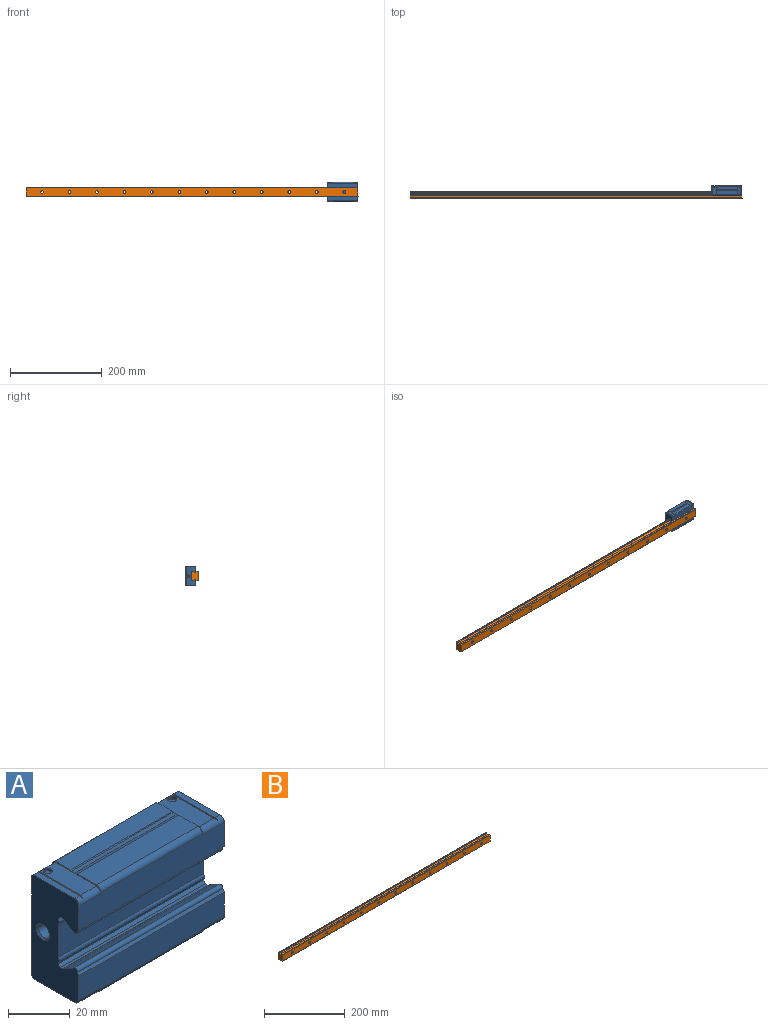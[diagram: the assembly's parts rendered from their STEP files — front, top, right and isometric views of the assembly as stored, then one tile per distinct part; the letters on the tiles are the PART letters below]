
ASSEMBLY  parts=2 mates=1
PART A: 104 faces, bbox 66.5x22x42 mm
  f0: plane 18.8x2.25mm, normal (0,0,1), area 42.3mm2, adj f1,f31,f77,f103
  f1: cylinder r=2mm len=9.95mm, axis (-1,0,0), area 30.8mm2, adj f0,f2,f29,f31,f41,f77,f100
  f2: plane 18.8x7.2mm, normal (0,0,1), area 128.3mm2, adj f1,f41,f86,f100,f102
  f3: plane 7.6x0.8mm, normal (0,0.71,-0.71), area 8.4mm2, adj f5,f8,f24,f41,f101
  f4: plane 2.25x0.8mm, normal (0,0.71,-0.71), area 2.5mm2, adj f7,f25,f31,f77
  f5: plane 18.8x7.2mm, normal (0,0,-1), area 128.3mm2, adj f3,f6,f41,f90,f101
  f6: cylinder r=2mm len=9.95mm, axis (-1,0,0), area 30.8mm2, adj f5,f7,f28,f31,f41,f77,f101
  f7: plane 18.8x2.25mm, normal (0,0,-1), area 42.3mm2, adj f4,f6,f31,f77
  f8: plane 40.4x0.5mm, normal (0.71,0.71,0), area 28.3mm2, adj f3,f24,f77,f100,f101,f102
  f9: plane 2.25x0.8mm, normal (0,0.71,-0.71), area 2.5mm2, adj f17,f26,f30,f76
  f10: plane 7.6x0.8mm, normal (0,0.71,-0.71), area 8.4mm2, adj f18,f19,f27,f42,f98
  f11: plane 7.6x0.8mm, normal (0,0.71,0.71), area 8.4mm2, adj f13,f19,f27,f42,f99
  f12: plane 2.25x0.8mm, normal (0,0.71,0.71), area 2.5mm2, adj f14,f26,f30,f76
  f13: plane 18.8x7.2mm, normal (0,0,1), area 128.3mm2, adj f11,f15,f42,f84,f99
  f14: plane 18.8x2.25mm, normal (0,0,1), area 42.3mm2, adj f12,f15,f30,f76
  f15: cylinder r=2mm len=9.95mm, axis (1,0,0), area 30.8mm2, adj f13,f14,f29,f30,f42,f76,f99
  f16: cylinder r=2mm len=9.95mm, axis (1,0,0), area 30.8mm2, adj f17,f18,f28,f30,f42,f76,f98
  f17: plane 18.8x2.25mm, normal (0,0,-1), area 42.3mm2, adj f9,f16,f30,f76
  f18: plane 18.8x7.2mm, normal (0,0,-1), area 128.3mm2, adj f10,f16,f42,f88,f98
  f19: plane 40.4x0.5mm, normal (-0.71,0.71,0), area 28.3mm2, adj f10,f11,f27,f76,f98,f99
  f20: plane 46.6x8.82mm, normal (0,0,1), area 411mm2, adj f33,f41,f42,f95
  f21: plane 46.6x7.1mm, normal (0,0,1), area 330.9mm2, adj f32,f41,f42,f97
  f22: plane 46.6x8.82mm, normal (0,0,-1), area 411mm2, adj f34,f41,f42,f93
  f23: plane 46.6x7.1mm, normal (0,0,-1), area 330.9mm2, adj f35,f41,f42,f94
  f24: plane 39.6x7.2mm, normal (0,1,0), area 285.1mm2, adj f3,f8,f41,f102
  f25: plane 39.6x2.25mm, normal (0,1,0), area 89.1mm2, adj f4,f31,f77,f103
  f26: plane 39.6x2.25mm, normal (0,1,0), area 89.1mm2, adj f9,f12,f30,f76
  f27: plane 39.6x7.2mm, normal (0,1,0), area 285.1mm2, adj f10,f11,f19,f42
  f28: plane 66.5x9.96mm, normal (0,-1,0), area 654.6mm2, adj f6,f16,f30,f31,f34,f41,f42,f55
  f29: plane 66.5x9.96mm, normal (0,-1,0), area 654.6mm2, adj f1,f15,f30,f31,f33,f41,f42,f56
  f30: plane 41.2x21.6mm, normal (-1,0,0), area 698.5mm2, adj f9,f12,f14,f15,f16,f17,f26,f28
  f31: plane 41.2x21.6mm, normal (1,0,0), area 698.5mm2, adj f0,f1,f4,f6,f7,f25,f28,f29
  f32: plane 46.6x1.1mm, normal (0,0.71,0.71), area 72.5mm2, adj f21,f40,f41,f42
  f33: cylinder r=2mm len=46.6mm, axis (1,0,0), area 146.4mm2, adj f20,f29,f41,f42
  f34: cylinder r=2mm len=46.6mm, axis (1,0,0), area 146.4mm2, adj f22,f28,f41,f42
  f35: plane 46.6x1.1mm, normal (0,0.71,-0.71), area 72.5mm2, adj f23,f36,f41,f42
  f36: plane 46.6x14.35mm, normal (0,1,0), area 629.4mm2, adj f35,f37,f41,f42,f49,f52
  f37: plane 46.6x0.3mm, normal (0,0.71,0.71), area 19.8mm2, adj f36,f38,f41,f42
  f38: plane 46.6x10.5mm, normal (0,1,0), area 489.3mm2, adj f37,f39,f41,f42
  f39: plane 46.6x0.3mm, normal (0,0.71,-0.71), area 19.8mm2, adj f38,f40,f41,f42
  f40: plane 46.6x14.35mm, normal (0,1,0), area 629.4mm2, adj f32,f39,f41,f42,f43,f46
  f41: plane 42x22mm, normal (1,0,0), area 28.8mm2, adj f1,f2,f3,f5,f6,f20,f21,f22
  f42: plane 42x22mm, normal (-1,0,0), area 28.8mm2, adj f10,f11,f13,f15,f16,f18,f20,f21
  f43: cone r=2.5mm half-angle=45deg, axis (0,1,0), area 8.8mm2, adj f40,f44
  f44: cylinder r=2.07mm len=9.17mm, axis (0,1,0), area 119.1mm2, adj f43,f45
  f45: cone r=2.07mm half-angle=60deg, axis (0,1,0), area 15.5mm2, adj f44
  f46: cone r=2.5mm half-angle=45deg, axis (0,1,0), area 8.8mm2, adj f40,f47
  f47: cylinder r=2.07mm len=9.17mm, axis (0,1,0), area 119.1mm2, adj f46,f48
  f48: cone r=2.07mm half-angle=60deg, axis (0,1,0), area 15.5mm2, adj f47
  f49: cone r=2.5mm half-angle=45deg, axis (0,1,0), area 8.8mm2, adj f36,f50
  f50: cylinder r=2.07mm len=9.17mm, axis (0,1,0), area 119.1mm2, adj f49,f51
  f51: cone r=2.07mm half-angle=60deg, axis (0,1,0), area 15.5mm2, adj f50
  f52: cone r=2.5mm half-angle=45deg, axis (0,1,0), area 8.8mm2, adj f36,f53
  f53: cylinder r=2.07mm len=9.17mm, axis (0,1,0), area 119.1mm2, adj f52,f54
  f54: cone r=2.07mm half-angle=60deg, axis (0,1,0), area 15.5mm2, adj f53
  f55: plane 66.5x0.92mm, normal (0,-0.8,0.6), area 76.7mm2, adj f28,f30,f31,f57
  f56: plane 66.5x0.92mm, normal (0,-0.8,-0.6), area 76.7mm2, adj f29,f30,f31,f75
  f57: cylinder r=1mm len=66.5mm, axis (1,0,0), area 165mm2, adj f30,f31,f55,f58
  f58: cylinder r=0.7mm len=66.5mm, axis (1,0,0), area 5.3mm2, adj f30,f31,f57,f59
  f59: plane 66.5x3.35mm, normal (0,0.5,0.87), area 257.1mm2, adj f30,f31,f58,f60
  f60: cylinder r=1.65mm len=66.5mm, axis (1,0,0), area 87.9mm2, adj f30,f31,f59,f61
  f61: plane 66.5x0.59mm, normal (0,0.5,0.87), area 45.2mm2, adj f30,f31,f60,f62
  f62: plane 66.5x1.16mm, normal (0,0,1), area 77.1mm2, adj f30,f31,f61,f63
  f63: plane 66.5x0.96mm, normal (0,-0.71,0.71), area 90.3mm2, adj f30,f31,f62,f64
  f64: plane 66.5x0.24mm, normal (0,-1,0), area 15.7mm2, adj f30,f31,f63,f65
  f65: cylinder r=1.65mm len=66.5mm, axis (1,0,0), area 169.8mm2, adj f30,f31,f64,f66
  f66: plane 66.5x12.99mm, normal (0,-1,0), area 864.1mm2, adj f30,f31,f65,f67
  f67: cylinder r=1.65mm len=66.5mm, axis (1,0,0), area 169.8mm2, adj f30,f31,f66,f68
  f68: plane 66.5x0.24mm, normal (0,-1,0), area 15.7mm2, adj f30,f31,f67,f69
  f69: plane 66.5x0.96mm, normal (0,-0.71,-0.71), area 90.3mm2, adj f30,f31,f68,f70
  f70: plane 66.5x1.16mm, normal (0,0,-1), area 77.1mm2, adj f30,f31,f69,f71
  f71: plane 66.5x0.59mm, normal (0,0.5,-0.87), area 45.2mm2, adj f30,f31,f70,f72
  f72: cylinder r=1.65mm len=66.5mm, axis (1,0,0), area 87.9mm2, adj f30,f31,f71,f73
  f73: plane 66.5x3.35mm, normal (0,0.5,-0.87), area 257.1mm2, adj f30,f31,f72,f74
  f74: cylinder r=0.7mm len=66.5mm, axis (1,0,0), area 5.3mm2, adj f30,f31,f73,f75
  f75: cylinder r=1mm len=66.5mm, axis (1,0,0), area 165mm2, adj f30,f31,f56,f74
  f76: plane 41.2x20.92mm, normal (1,0,0), area 40mm2, adj f9,f12,f14,f15,f16,f17,f19,f26
  f77: plane 41.2x20.92mm, normal (-1,0,0), area 40mm2, adj f0,f1,f4,f6,f7,f8,f25,f100
  f78: cone r=866.03mm half-angle=60deg, axis (1,0,0), area 21.9mm2, adj f79
  f79: cylinder r=2.46mm len=5.46mm, axis (-1,0,0), area 84.3mm2, adj f78,f80
  f80: cone r=2.46mm half-angle=45deg, axis (1,0,0), area 13.1mm2, adj f31,f79
  f81: cone r=3mm half-angle=45deg, axis (-1,0,0), area 13.1mm2, adj f30,f82
  f82: cylinder r=2.46mm len=5.46mm, axis (-1,0,0), area 84.3mm2, adj f81,f83
  f83: cone r=2.46mm half-angle=60deg, axis (-1,0,0), area 21.9mm2, adj f82
  f84: cylinder r=1.5mm len=3mm, axis (0,0,-1), area 9.4mm2, adj f13,f85
  f85: plane 3x3mm, normal (0,0,1), area 7.1mm2, adj f84
  f86: cylinder r=1.5mm len=3mm, axis (0,0,-1), area 9.4mm2, adj f2,f87
  f87: plane 3x3mm, normal (0,0,1), area 7.1mm2, adj f86
  f88: cylinder r=1.5mm len=3mm, axis (0,0,1), area 9.4mm2, adj f18,f89
  f89: plane 3x3mm, normal (0,0,-1), area 7.1mm2, adj f88
  f90: cylinder r=1.5mm len=3mm, axis (0,0,1), area 9.4mm2, adj f5,f91
  f91: plane 3x3mm, normal (0,0,-1), area 7.1mm2, adj f90
  f92: plane 46.6x1.5mm, normal (0,0,-1), area 69.7mm2, adj f41,f42,f93,f94
  f93: plane 46.6x1.17mm, normal (0,0.26,-0.97), area 56.5mm2, adj f22,f41,f42,f92
  f94: cylinder r=0.32mm len=46.6mm, axis (1,0,0), area 23.1mm2, adj f23,f41,f42,f92
  f95: plane 46.6x1.17mm, normal (0,0.26,0.97), area 56.5mm2, adj f20,f41,f42,f96
  f96: plane 46.6x1.5mm, normal (0,0,1), area 69.7mm2, adj f41,f42,f95,f97
  f97: cylinder r=0.32mm len=46.6mm, axis (1,0,0), area 23.1mm2, adj f21,f41,f42,f96
  f98: plane 20.52x0.5mm, normal (-0.71,0,-0.71), area 14.1mm2, adj f10,f16,f18,f19,f76
  f99: plane 20.52x0.5mm, normal (-0.71,0,0.71), area 14.1mm2, adj f11,f13,f15,f19,f76
  f100: plane 20.52x0.5mm, normal (0.71,0,0.71), area 14.1mm2, adj f1,f2,f8,f77,f102
  f101: plane 20.52x0.5mm, normal (0.71,0,-0.71), area 14.1mm2, adj f3,f5,f6,f8,f77
  f102: plane 7.6x0.8mm, normal (0,0.71,0.71), area 8.4mm2, adj f2,f8,f24,f41,f100
  f103: plane 2.25x0.8mm, normal (0,0.71,0.71), area 2.5mm2, adj f0,f25,f31,f77
PART B: 64 faces, bbox 725x15.5x20 mm
  f0: plane 725x3.35mm, normal (0,-0.5,0.87), area 2803.4mm2, adj f16,f22,f23,f63
  f1: plane 725x4.09mm, normal (0,0,1), area 2965.2mm2, adj f2,f17,f23,f63
  f2: plane 725x1.18mm, normal (0,-0.71,0.71), area 1209.9mm2, adj f1,f9,f23,f63
  f3: plane 725x12.99mm, normal (0,1,0), area 8569.6mm2, adj f23,f24,f27,f30,f33,f36,f39,f42
  f4: plane 725x0.59mm, normal (0,-0.5,-0.87), area 492.9mm2, adj f5,f23,f60,f63
  f5: plane 725x1.16mm, normal (0,0,-1), area 841mm2, adj f4,f10,f23,f63
  f6: plane 725x3.35mm, normal (0,-0.5,-0.87), area 2803.4mm2, adj f19,f23,f60,f63
  f7: plane 725x4.09mm, normal (0,0,-1), area 2965.2mm2, adj f8,f21,f23,f63
  f8: plane 725x1.18mm, normal (0,-0.71,-0.71), area 1209.9mm2, adj f7,f9,f23,f63
  f9: plane 725x17.64mm, normal (0,-1,0), area 12449.7mm2, adj f2,f8,f23,f26,f29,f32,f35,f38
  f10: plane 725x0.96mm, normal (0,0.71,-0.71), area 984.3mm2, adj f5,f11,f23,f63
  f11: plane 725x0.24mm, normal (0,1,0), area 171.6mm2, adj f10,f23,f61,f63
  f12: plane 725x0.24mm, normal (0,1,0), area 171.6mm2, adj f13,f23,f62,f63
  f13: plane 725x0.96mm, normal (0,0.71,0.71), area 984.3mm2, adj f12,f14,f23,f63
  f14: plane 725x1.16mm, normal (0,0,1), area 841mm2, adj f13,f15,f23,f63
  f15: plane 725x0.59mm, normal (0,-0.5,0.87), area 492.9mm2, adj f14,f22,f23,f63
  f16: cylinder r=0.7mm len=725mm, axis (1,0,0), area 58.1mm2, adj f0,f18,f23,f63
  f17: plane 725x1.88mm, normal (0,0.8,0.6), area 1712.5mm2, adj f1,f18,f23,f63
  f18: cylinder r=1mm len=725mm, axis (1,0,0), area 1798.4mm2, adj f16,f17,f23,f63
  f19: cylinder r=0.7mm len=725mm, axis (1,0,0), area 58.1mm2, adj f6,f20,f23,f63
  f20: cylinder r=1mm len=725mm, axis (1,0,0), area 1798.4mm2, adj f19,f21,f23,f63
  f21: plane 725x1.88mm, normal (0,0.8,-0.6), area 1712.5mm2, adj f7,f20,f23,f63
  f22: cylinder r=1.65mm len=725mm, axis (1,0,0), area 958.2mm2, adj f0,f15,f23,f63
  f23: plane 20x15.5mm, normal (-1,0,0), area 278.7mm2, adj f0,f1,f2,f3,f4,f5,f6,f7
  f24: cylinder r=4.75mm len=9.5mm, axis (0,1,0), area 253.7mm2, adj f3,f25
  f25: plane 9.5x9.5mm, normal (0,1,0), area 42.6mm2, adj f24,f26
  f26: cylinder r=3mm len=7mm, axis (0,1,0), area 131.9mm2, adj f9,f25
  f27: cylinder r=4.75mm len=9.5mm, axis (0,1,0), area 253.7mm2, adj f3,f28
  f28: plane 9.5x9.5mm, normal (0,1,0), area 42.6mm2, adj f27,f29
  f29: cylinder r=3mm len=7mm, axis (0,1,0), area 131.9mm2, adj f9,f28
  f30: cylinder r=4.75mm len=9.5mm, axis (0,1,0), area 253.7mm2, adj f3,f31
  f31: plane 9.5x9.5mm, normal (0,1,0), area 42.6mm2, adj f30,f32
  f32: cylinder r=3mm len=7mm, axis (0,1,0), area 131.9mm2, adj f9,f31
  f33: cylinder r=4.75mm len=9.5mm, axis (0,1,0), area 253.7mm2, adj f3,f34
  f34: plane 9.5x9.5mm, normal (0,1,0), area 42.6mm2, adj f33,f35
  f35: cylinder r=3mm len=7mm, axis (0,1,0), area 131.9mm2, adj f9,f34
  f36: cylinder r=4.75mm len=9.5mm, axis (0,1,0), area 253.7mm2, adj f3,f37
  f37: plane 9.5x9.5mm, normal (0,1,0), area 42.6mm2, adj f36,f38
  f38: cylinder r=3mm len=7mm, axis (0,1,0), area 131.9mm2, adj f9,f37
  f39: cylinder r=4.75mm len=9.5mm, axis (0,1,0), area 253.7mm2, adj f3,f40
  f40: plane 9.5x9.5mm, normal (0,1,0), area 42.6mm2, adj f39,f41
  f41: cylinder r=3mm len=7mm, axis (0,1,0), area 131.9mm2, adj f9,f40
  f42: cylinder r=4.75mm len=9.5mm, axis (0,1,0), area 253.7mm2, adj f3,f43
  f43: plane 9.5x9.5mm, normal (0,1,0), area 42.6mm2, adj f42,f44
  f44: cylinder r=3mm len=7mm, axis (0,1,0), area 131.9mm2, adj f9,f43
  f45: cylinder r=4.75mm len=9.5mm, axis (0,1,0), area 253.7mm2, adj f3,f46
  f46: plane 9.5x9.5mm, normal (0,1,0), area 42.6mm2, adj f45,f47
  f47: cylinder r=3mm len=7mm, axis (0,1,0), area 131.9mm2, adj f9,f46
  f48: cylinder r=4.75mm len=9.5mm, axis (0,1,0), area 253.7mm2, adj f3,f49
  f49: plane 9.5x9.5mm, normal (0,1,0), area 42.6mm2, adj f48,f50
  f50: cylinder r=3mm len=7mm, axis (0,1,0), area 131.9mm2, adj f9,f49
  f51: cylinder r=4.75mm len=9.5mm, axis (0,1,0), area 253.7mm2, adj f3,f52
  f52: plane 9.5x9.5mm, normal (0,1,0), area 42.6mm2, adj f51,f53
  f53: cylinder r=3mm len=7mm, axis (0,1,0), area 131.9mm2, adj f9,f52
  f54: cylinder r=4.75mm len=9.5mm, axis (0,1,0), area 253.7mm2, adj f3,f55
  f55: plane 9.5x9.5mm, normal (0,1,0), area 42.6mm2, adj f54,f56
  f56: cylinder r=3mm len=7mm, axis (0,1,0), area 131.9mm2, adj f9,f55
  f57: cylinder r=4.75mm len=9.5mm, axis (0,1,0), area 253.7mm2, adj f3,f58
  f58: plane 9.5x9.5mm, normal (0,1,0), area 42.6mm2, adj f57,f59
  f59: cylinder r=3mm len=7mm, axis (0,1,0), area 131.9mm2, adj f9,f58
  f60: cylinder r=1.65mm len=725mm, axis (1,0,0), area 958.2mm2, adj f4,f6,f23,f63
  f61: cylinder r=1.65mm len=725mm, axis (1,0,0), area 1851.7mm2, adj f3,f11,f23,f63
  f62: cylinder r=1.65mm len=725mm, axis (1,0,0), area 1851.7mm2, adj f3,f12,f23,f63
  f63: plane 20x15.5mm, normal (1,0,0), area 278.7mm2, adj f0,f1,f2,f3,f4,f5,f6,f7
PLACE A t=(538.88,49.78,0.85)mm
PLACE B t=(-117.87,43.78,0.85)mm
MATE slider B.f63 <-> A.f31  axis (1,0,0) through (572.13,59.28,0.85)mm
